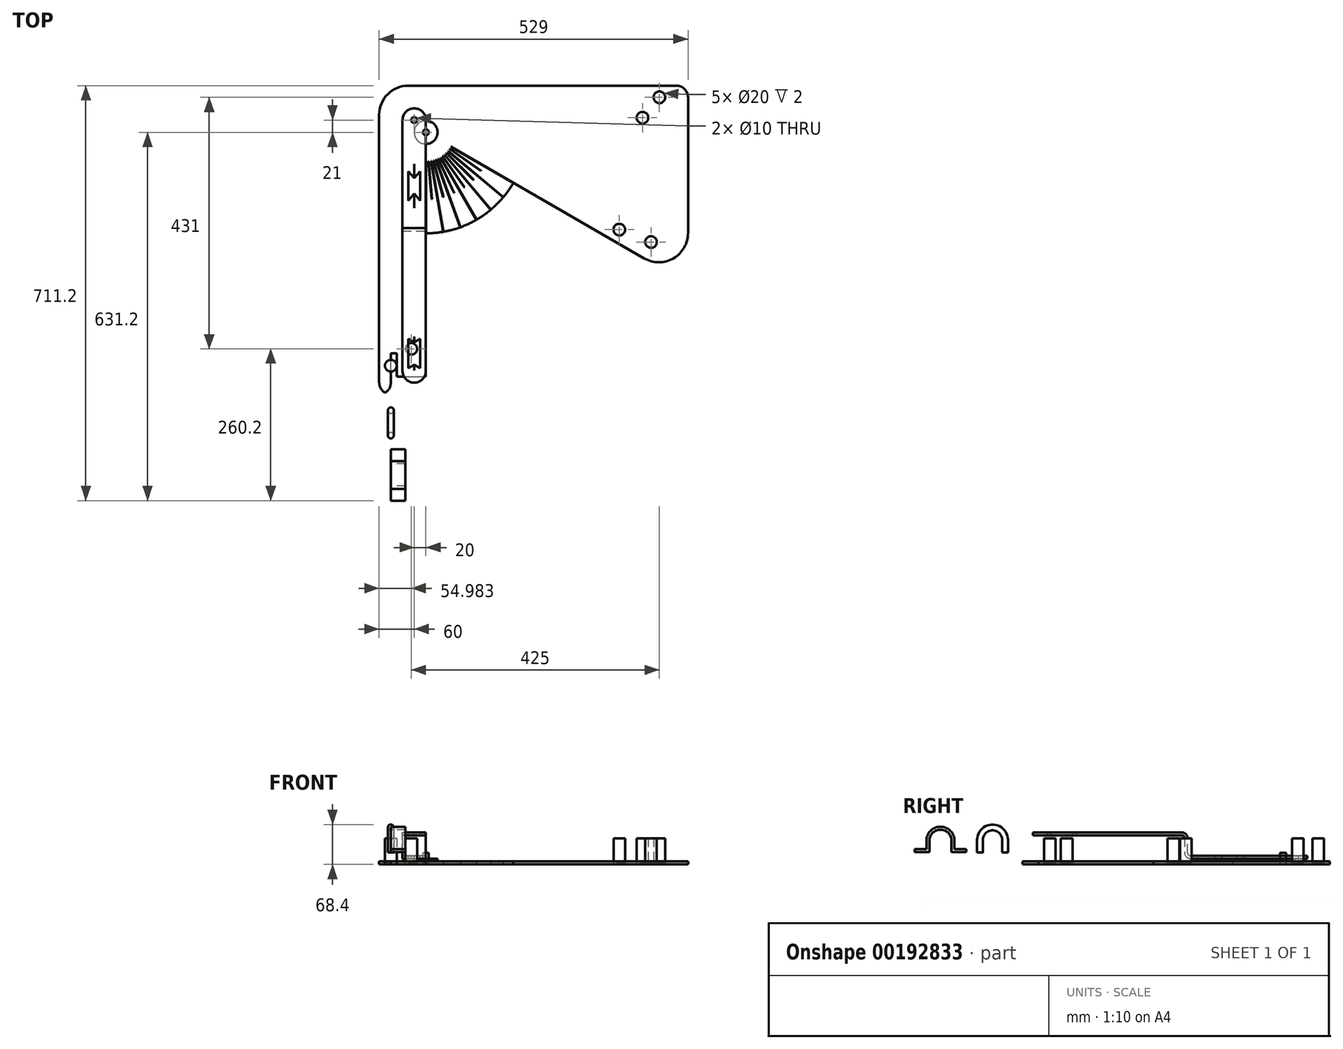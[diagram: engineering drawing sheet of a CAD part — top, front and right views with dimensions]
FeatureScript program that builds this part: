
annotation { "Feature Type Name" : "Feature", "Feature Type Description" : "" }
export const myFeature = defineFeature(function(context is Context, id is Id, definition is map)
    precondition{}
    {
        {
            var Q0;
            Q0=qCreatedBy(makeId("Top.planeOp"),FACE);
            var sketch = newSketch(context, id + "F0", { "sketchPlane" : qUnion([Q0])});
            skLineSegment(sketch, "E0.bottom", {"start": v(0, 0) * mm, "end": v(489, 0) * mm});
            skLineSegment(sketch, "E0.left", {"start": v(0, 0) * mm, "end": v(0, 500) * mm});
            skLineSegment(sketch, "E0.right", {"start": v(489, 0) * mm, "end": v(489, 479) * mm});
            skLineSegment(sketch, "E1.top", {"start": v(0, 0) * mm, "end": v(10, 0) * mm});
            skLineSegment(sketch, "E1.left", {"start": v(0, 489) * mm, "end": v(0, 0) * mm});
            skLineSegment(sketch, "E1.right", {"start": v(10, 50) * mm, "end": v(10, 10) * mm});
            skPoint(sketch, "E2", {"position": v(60, 429) * mm});
            skLineSegment(sketch, "E3", {"start": v(60, 255.9) * mm, "end": v(60, 0) * mm});
            skLineSegment(sketch, "E4", {"start": v(209.9, 342.45) * mm, "end": v(489, 181.32) * mm});
            skLineSegment(sketch, "E5.bottom", {"start": v(10, 48) * mm, "end": v(60, 48) * mm, "construction": true});
            skLineSegment(sketch, "E5.right", {"start": v(60, 48) * mm, "end": v(60, 10) * mm, "construction": true});
            skLineSegment(sketch, "E6.top", {"start": v(441, 429) * mm, "end": v(479, 429) * mm, "construction": true});
            skLineSegment(sketch, "E6.left", {"start": v(441, 479) * mm, "end": v(441, 429) * mm, "construction": true});
            skArc(sketch, "E7", {"start": v(60, 29) * mm, "mid": v(342.84, 146.16) * mm, "end": v(460, 429) * mm, "construction": true});
            skPoint(sketch, "E8", {"position": v(10, 29) * mm});
            skPoint(sketch, "E9", {"position": v(460, 479) * mm});
            skArc(sketch, "E10.0", {"start": v(60, 10) * mm, "mid": v(356.28, 132.72) * mm, "end": v(479, 429) * mm, "construction": true});
            skArc(sketch, "E11.0", {"start": v(60, 48) * mm, "mid": v(329.4, 159.6) * mm, "end": v(441, 429) * mm, "construction": true});
            skLineSegment(sketch, "E12", {"start": v(60, 255.9) * mm, "end": v(209.9, 342.45) * mm, "construction": true});
            skPoint(sketch, "E13.end.orphan", {"position": v(189.9, 354) * mm});
            skPoint(sketch, "E13.start.orphan", {"position": v(60, 279) * mm});
            skCircle(sketch, "E14", {"center": v(60, 429) * mm, "radius": 5 * mm});
            skLineSegment(sketch, "E15.top", {"start": v(489, 489) * mm, "end": v(0, 489) * mm});
            skLineSegment(sketch, "E15.left", {"start": v(489, 479) * mm, "end": v(489, 489) * mm});
            skLineSegment(sketch, "E16", {"start": v(439, 489) * mm, "end": v(439, 479) * mm});
            skLineSegment(sketch, "E17", {"start": v(439, 479) * mm, "end": v(479, 479) * mm});
            skLineSegment(sketch, "E18", {"start": v(479, 479) * mm, "end": v(479, 429) * mm});
            skLineSegment(sketch, "E19", {"start": v(489, 429) * mm, "end": v(479, 429) * mm});
            skArc(sketch, "E20", {"start": v(60, 255.9) * mm, "mid": v(146.55, 279.1) * mm, "end": v(209.9, 342.45) * mm});
            skLineSegment(sketch, "E21", {"start": v(0, 50) * mm, "end": v(10, 50) * mm});
            skLineSegment(sketch, "E22", {"start": v(10, 10) * mm, "end": v(60, 10) * mm});
            skLineSegment(sketch, "E23", {"start": v(60, 0) * mm, "end": v(60, -20) * mm});
            skLineSegment(sketch, "E24", {"start": v(60, -20) * mm, "end": v(0, -20) * mm});
            skLineSegment(sketch, "E25", {"start": v(0, -20) * mm, "end": v(0, 0) * mm});
            skLineSegment(sketch, "E26", {"start": v(0, 489) * mm, "end": v(-20, 489) * mm});
            skLineSegment(sketch, "E27", {"start": v(-20, 489) * mm, "end": v(-20, -20) * mm});
            skLineSegment(sketch, "E28", {"start": v(-20, -20) * mm, "end": v(0, -20) * mm});
            skLineSegment(sketch, "E29", {"start": v(489, 181.32) * mm, "end": v(509, 169.77) * mm});
            skLineSegment(sketch, "E30", {"start": v(509, 169.77) * mm, "end": v(509, 489) * mm});
            skLineSegment(sketch, "E31", {"start": v(509, 489) * mm, "end": v(489, 489) * mm});
            skLineSegment(sketch, "E32", {"start": v(509, 489) * mm, "end": v(509, 509) * mm});
            skLineSegment(sketch, "E33", {"start": v(509, 509) * mm, "end": v(-20, 509) * mm});
            skLineSegment(sketch, "E34", {"start": v(-20, 509) * mm, "end": v(-20, 489) * mm});
            skSolve(sketch);
        }
        {
            var Q0;
            {var subQ3=sQuery(id+"F0.wireOp",EDGE,"E1.right");Q0=makeQuery(id+"F0.imprint","IMPRINT",FACE,{"disambiguationData":[TD([[makeQuery(id+"F0.imprint","IMPRINT",EDGE,{"derivedFrom":subQ3}),1.0]])]});}
            var Q1;
            {var subQ2=sQuery(id+"F0.wireOp",EDGE,"E1.top");Q1=makeQuery(id+"F0.imprint","IMPRINT",FACE,{"disambiguationData":[TD([[makeQuery(id+"F0.imprint","IMPRINT",EDGE,{"derivedFrom":subQ2}),1.0]])]});}
            var Q2;
            {var subQ1=sQuery(id+"F0.wireOp",EDGE,"E15.left");Q2=makeQuery(id+"F0.imprint","IMPRINT",FACE,{"disambiguationData":[TD([[makeQuery(id+"F0.imprint","IMPRINT",EDGE,{"derivedFrom":subQ1}),1.0]])]});}
            var Q3;
            {var subQ1=sQuery(id+"F0.wireOp",EDGE,"E25");Q3=makeQuery(id+"F0.imprint","IMPRINT",FACE,{"disambiguationData":[TD([[makeQuery(id+"F0.imprint","IMPRINT",EDGE,{"derivedFrom":subQ1}),1.0]])]});}
            var Q4;
            {var subQ0=sQuery(id+"F0.wireOp",EDGE,"E1.top");Q4=makeQuery(id+"F0.imprint","IMPRINT",FACE,{"disambiguationData":[TD([[makeQuery(id+"F0.imprint","IMPRINT",EDGE,{"derivedFrom":subQ0}),-1.0]])]});}
            var Q5;
            {var subQ3=sQuery(id+"F0.wireOp",EDGE,"E26");Q5=makeQuery(id+"F0.imprint","IMPRINT",FACE,{"disambiguationData":[TD([[makeQuery(id+"F0.imprint","IMPRINT",EDGE,{"derivedFrom":subQ3}),-1.0]])]});}
            var Q6;
            {var subQ1=sQuery(id+"F0.wireOp",EDGE,"E15.left");Q6=makeQuery(id+"F0.imprint","IMPRINT",FACE,{"disambiguationData":[TD([[makeQuery(id+"F0.imprint","IMPRINT",EDGE,{"derivedFrom":subQ1}),-1.0]])]});}
            extrude(context, id + "F1", {"entities" : qUnion([Q0, Q1, Q2, Q3, Q4, Q5, Q6]), "depth" : 5 * mm});
        }
        {
            var Q0;
            Q0=makeQuery(id+"F1.opExtrude","SWEPT_FACE",FACE,{"disambiguationData":[OSD([sQuery(id+"F0.wireOp",EDGE,"E33")])]});
            cPlane(context, id + "F2", {"entities" : qUnion([Q0]), "cplaneType" : CPlaneType.OFFSET, "offset" : 80 * mm, "oppositeDirection" : true, "width" : 150 * mm, "height" : 150 * mm});
        }
        {
            var Q0;
            Q0=qCreatedBy(id+"F2.planeOp",FACE);
            var sketch = newSketch(context, id + "F3", { "sketchPlane" : qUnion([Q0])});
            skLineSegment(sketch, "E35", {"start": v(-60, 20) * mm, "end": v(-60, 0) * mm});
            skLineSegment(sketch, "E36", {"start": v(-60, 20) * mm, "end": v(-65, 20) * mm});
            skLineSegment(sketch, "E37", {"start": v(-65, 20) * mm, "end": v(-65, 10) * mm});
            skLineSegment(sketch, "E38", {"start": v(-65, 10) * mm, "end": v(-80, 10) * mm});
            skLineSegment(sketch, "E39", {"start": v(-80, 10) * mm, "end": v(-80, 5) * mm});
            skLineSegment(sketch, "E40", {"start": v(-80, 5) * mm, "end": v(-65, 5) * mm});
            skLineSegment(sketch, "E41", {"start": v(-65, 5) * mm, "end": v(-65, 0) * mm});
            skLineSegment(sketch, "E42", {"start": v(-65, 0) * mm, "end": v(-60, 0) * mm});
            skSolve(sketch);
        }
        {
            var Q0;
            Q0=qSketchRegion(id+"F3",true);
            var Q1;
            Q1=sQuery(id+"F3.wireOp",EDGE,"E35");
            revolve(context, id + "F4", {"entities" : qUnion([Q0]), "axis" : qUnion([Q1]), "revolveType" : RevolveType.FULL});
        }
        {
            var Q0;
            Q0=makeQuery(id+"F1.opExtrude","CAP_FACE",FACE,{"disambiguationData":[OSD([sQuery(id+"F0.wireOp",EDGE,"E0.bottom"),sQuery(id+"F0.wireOp",EDGE,"E0.top"),sQuery(id+"F0.wireOp",EDGE,"E0.right"),sQuery(id+"F0.wireOp",EDGE,"E1.right"),sQuery(id+"F0.wireOp",EDGE,"E3"),sQuery(id+"F0.wireOp",EDGE,"E4"),sQuery(id+"F0.wireOp",EDGE,"E12"),sQuery(id+"F0.wireOp",EDGE,"E14")])],"isStart":false});
            cPlane(context, id + "F5", {"entities" : qUnion([Q0]), "cplaneType" : CPlaneType.OFFSET, "offset" : 0 * mm, "width" : 150 * mm, "height" : 150 * mm});
        }
        {
            var Q0;
            Q0=qCreatedBy(id+"F5.planeOp",FACE);
            var sketch = newSketch(context, id + "F6", { "sketchPlane" : qUnion([Q0])});
            skCircle(sketch, "E43", {"center": v(34.98, 58) * mm, "radius": 10 * mm});
            skLineSegment(sketch, "E44.bottom", {"start": v(9.98, 10) * mm, "end": v(59.98, 10) * mm, "construction": true});
            skLineSegment(sketch, "E44.top", {"start": v(9.98, 48) * mm, "end": v(59.98, 48) * mm, "construction": true});
            skLineSegment(sketch, "E44.left", {"start": v(9.98, 10) * mm, "end": v(9.98, 48) * mm, "construction": true});
            skLineSegment(sketch, "E44.right", {"start": v(59.98, 10) * mm, "end": v(59.98, 48) * mm, "construction": true});
            skLineSegment(sketch, "E45.bottom", {"start": v(478.98, 479) * mm, "end": v(440.98, 479) * mm, "construction": true});
            skLineSegment(sketch, "E45.top", {"start": v(478.98, 429) * mm, "end": v(440.98, 429) * mm, "construction": true});
            skLineSegment(sketch, "E45.left", {"start": v(478.98, 479) * mm, "end": v(478.98, 429) * mm, "construction": true});
            skLineSegment(sketch, "E45.right", {"start": v(440.98, 479) * mm, "end": v(440.98, 429) * mm, "construction": true});
            skArc(sketch, "E46", {"start": v(59.98, 29) * mm, "mid": v(342.83, 146.16) * mm, "end": v(459.98, 429) * mm, "construction": true});
            skArc(sketch, "E47.0", {"start": v(59.98, 10) * mm, "mid": v(356.26, 132.72) * mm, "end": v(478.98, 429) * mm, "construction": true});
            skArc(sketch, "E48.0", {"start": v(59.98, 48) * mm, "mid": v(329.4, 159.6) * mm, "end": v(440.98, 429) * mm, "construction": true});
            skLineSegment(sketch, "E49", {"start": v(459.98, 429) * mm, "end": v(459.98, 479) * mm, "construction": true});
            skLineSegment(sketch, "E50", {"start": v(59.98, 29) * mm, "end": v(9.98, 29) * mm, "construction": true});
            skCircle(sketch, "E51", {"center": v(430.98, 454) * mm, "radius": 10 * mm});
            skCircle(sketch, "E52", {"center": v(445.6, 241.01) * mm, "radius": 10 * mm});
            skLineSegment(sketch, "E53", {"start": v(445.6, 241.01) * mm, "end": v(391.37, 262.2) * mm, "construction": true});
            skCircle(sketch, "E54", {"center": v(391.37, 262.2) * mm, "radius": 10 * mm});
            skCircle(sketch, "E55.MirrorC", {"center": v(34.98, 0) * mm, "radius": 10 * mm});
            skCircle(sketch, "E56", {"center": v(-0.02, 29) * mm, "radius": 10 * mm});
            skLineSegment(sketch, "E57", {"start": v(34.98, 0) * mm, "end": v(34.98, 48) * mm, "construction": true});
            skCircle(sketch, "E58.MirrorC", {"center": v(488.98, 454) * mm, "radius": 10 * mm});
            skLineSegment(sketch, "E59", {"start": v(430.98, 454) * mm, "end": v(488.98, 454) * mm, "construction": true});
            skCircle(sketch, "E60", {"center": v(459.98, 489) * mm, "radius": 10 * mm});
            skSolve(sketch);
        }
        {
            var Q0;
            Q0=makeQuery(id+"F6.imprint","IMPRINT",FACE,{"disambiguationData":[TD([[makeQuery(id+"F6.imprint","IMPRINT",EDGE,{"derivedFrom":sQuery(id+"F6.wireOp",EDGE,"E58.MirrorC")}),-1.0]])]});
            var Q1;
            Q1=makeQuery(id+"F6.imprint","IMPRINT",FACE,{"disambiguationData":[TD([[makeQuery(id+"F6.imprint","IMPRINT",EDGE,{"derivedFrom":sQuery(id+"F6.wireOp",EDGE,"E60")}),1.0]])]});
            var Q2;
            Q2=makeQuery(id+"F6.imprint","IMPRINT",FACE,{"disambiguationData":[TD([[makeQuery(id+"F6.imprint","IMPRINT",EDGE,{"derivedFrom":sQuery(id+"F6.wireOp",EDGE,"E51")}),1.0]])]});
            var Q3;
            Q3=makeQuery(id+"F6.imprint","IMPRINT",FACE,{"disambiguationData":[TD([[makeQuery(id+"F6.imprint","IMPRINT",EDGE,{"derivedFrom":sQuery(id+"F6.wireOp",EDGE,"E52")}),1.0]])]});
            var Q4;
            Q4=makeQuery(id+"F6.imprint","IMPRINT",FACE,{"disambiguationData":[TD([[makeQuery(id+"F6.imprint","IMPRINT",EDGE,{"derivedFrom":sQuery(id+"F6.wireOp",EDGE,"E54")}),1.0]])]});
            var Q5;
            Q5=makeQuery(id+"F6.imprint","IMPRINT",FACE,{"disambiguationData":[TD([[makeQuery(id+"F6.imprint","IMPRINT",EDGE,{"derivedFrom":sQuery(id+"F6.wireOp",EDGE,"E55.MirrorC")}),-1.0]])]});
            var Q6;
            Q6=makeQuery(id+"F6.imprint","IMPRINT",FACE,{"disambiguationData":[TD([[makeQuery(id+"F6.imprint","IMPRINT",EDGE,{"derivedFrom":sQuery(id+"F6.wireOp",EDGE,"E43")}),1.0]])]});
            var Q7;
            Q7=makeQuery(id+"F6.imprint","IMPRINT",FACE,{"disambiguationData":[TD([[makeQuery(id+"F6.imprint","IMPRINT",EDGE,{"derivedFrom":sQuery(id+"F6.wireOp",EDGE,"E56")}),1.0]])]});
            extrude(context, id + "F7", {"entities" : qUnion([Q0, Q1, Q2, Q3, Q4, Q5, Q6, Q7]), "operationType" : NewBodyOperationType.REMOVE, "oppositeDirection" : true, "depth" : 2 * mm});
        }
        {
            var Q0;
            Q0=makeQuery(id+"F6.imprint","IMPRINT",FACE,{"disambiguationData":[TD([[makeQuery(id+"F6.imprint","IMPRINT",EDGE,{"derivedFrom":sQuery(id+"F6.wireOp",EDGE,"E58.MirrorC")}),-1.0]])]});
            var Q1;
            Q1=makeQuery(id+"F6.imprint","IMPRINT",FACE,{"disambiguationData":[TD([[makeQuery(id+"F6.imprint","IMPRINT",EDGE,{"derivedFrom":sQuery(id+"F6.wireOp",EDGE,"E60")}),1.0]])]});
            var Q2;
            Q2=makeQuery(id+"F6.imprint","IMPRINT",FACE,{"disambiguationData":[TD([[makeQuery(id+"F6.imprint","IMPRINT",EDGE,{"derivedFrom":sQuery(id+"F6.wireOp",EDGE,"E51")}),1.0]])]});
            var Q3;
            Q3=makeQuery(id+"F6.imprint","IMPRINT",FACE,{"disambiguationData":[TD([[makeQuery(id+"F6.imprint","IMPRINT",EDGE,{"derivedFrom":sQuery(id+"F6.wireOp",EDGE,"E52")}),1.0]])]});
            var Q4;
            Q4=makeQuery(id+"F6.imprint","IMPRINT",FACE,{"disambiguationData":[TD([[makeQuery(id+"F6.imprint","IMPRINT",EDGE,{"derivedFrom":sQuery(id+"F6.wireOp",EDGE,"E54")}),1.0]])]});
            var Q5;
            Q5=makeQuery(id+"F6.imprint","IMPRINT",FACE,{"disambiguationData":[TD([[makeQuery(id+"F6.imprint","IMPRINT",EDGE,{"derivedFrom":sQuery(id+"F6.wireOp",EDGE,"E56")}),1.0]])]});
            var Q6;
            Q6=makeQuery(id+"F6.imprint","IMPRINT",FACE,{"disambiguationData":[TD([[makeQuery(id+"F6.imprint","IMPRINT",EDGE,{"derivedFrom":sQuery(id+"F6.wireOp",EDGE,"E55.MirrorC")}),-1.0]])]});
            var Q7;
            Q7=makeQuery(id+"F6.imprint","IMPRINT",FACE,{"disambiguationData":[TD([[makeQuery(id+"F6.imprint","IMPRINT",EDGE,{"derivedFrom":sQuery(id+"F6.wireOp",EDGE,"E43")}),1.0]])]});
            extrude(context, id + "F8", {"entities" : qUnion([Q0, Q1, Q2, Q3, Q4, Q5, Q6, Q7]), "depth" : 40 * mm});
        }
        {
            var Q0;
            Q0=makeQuery(id+"F1.opExtrude","CAP_FACE",FACE,{"disambiguationData":[OSD([sQuery(id+"F0.wireOp",EDGE,"E0.bottom"),sQuery(id+"F0.wireOp",EDGE,"E0.right"),sQuery(id+"F0.wireOp",EDGE,"E1.right"),sQuery(id+"F0.wireOp",EDGE,"E3"),sQuery(id+"F0.wireOp",EDGE,"E4"),sQuery(id+"F0.wireOp",EDGE,"E12"),sQuery(id+"F0.wireOp",EDGE,"E14"),sQuery(id+"F0.wireOp",EDGE,"E15.top"),sQuery(id+"F0.wireOp",EDGE,"E16"),sQuery(id+"F0.wireOp",EDGE,"E17"),sQuery(id+"F0.wireOp",EDGE,"E18"),sQuery(id+"F0.wireOp",EDGE,"E19")])],"isStart":false});
            var sketch = newSketch(context, id + "F9", { "sketchPlane" : qUnion([Q0])});
            skLineSegment(sketch, "E61", {"start": v(60, 379) * mm, "end": v(60, 255.9) * mm});
            skLineSegment(sketch, "E62", {"start": v(103.3, 404) * mm, "end": v(209.9, 342.45) * mm});
            skArc(sketch, "E63", {"start": v(60, 314) * mm, "mid": v(117.5, 329.4) * mm, "end": v(159.6, 371.5) * mm});
            skLineSegment(sketch, "E64.0", {"start": v(64.45, 426.72) * mm, "end": v(210.03, 342.67) * mm});
            skArc(sketch, "E65", {"start": v(60, 424) * mm, "mid": v(62.6, 424.73) * mm, "end": v(64.45, 426.72) * mm});
            skLineSegment(sketch, "E66.trimOffspring", {"start": v(64.2, 426.29) * mm, "end": v(64.83, 425.92) * mm});
            skLineSegment(sketch, "E67", {"start": v(210.03, 342.67) * mm, "end": v(209.9, 342.45) * mm});
            skLineSegment(sketch, "E68", {"start": v(100.96, 400.32) * mm, "end": v(154.2, 363.04) * mm});
            skLineSegment(sketch, "E69", {"start": v(98.3, 396.86) * mm, "end": v(192.6, 317.74) * mm});
            skLineSegment(sketch, "E70", {"start": v(95.36, 393.64) * mm, "end": v(141.32, 347.68) * mm});
            skLineSegment(sketch, "E71", {"start": v(92.14, 390.7) * mm, "end": v(171.26, 296.4) * mm});
            skLineSegment(sketch, "E72", {"start": v(88.68, 388.04) * mm, "end": v(125.96, 334.8) * mm});
            skLineSegment(sketch, "E73", {"start": v(85, 385.7) * mm, "end": v(146.55, 279.1) * mm});
            skLineSegment(sketch, "E74", {"start": v(81.13, 383.68) * mm, "end": v(108.6, 324.77) * mm});
            skLineSegment(sketch, "E75", {"start": v(77.1, 382.02) * mm, "end": v(119.2, 266.34) * mm});
            skLineSegment(sketch, "E76", {"start": v(72.94, 380.7) * mm, "end": v(89.76, 317.92) * mm});
            skLineSegment(sketch, "E77", {"start": v(68.68, 379.76) * mm, "end": v(90.06, 258.54) * mm});
            skLineSegment(sketch, "E78", {"start": v(64.36, 379.2) * mm, "end": v(70.02, 314.44) * mm});
            skArc(sketch, "E79", {"start": v(60, 255.9) * mm, "mid": v(146.55, 279.1) * mm, "end": v(209.9, 342.45) * mm, "construction": true});
            skPoint(sketch, "E80.orphan", {"position": v(117.5, 329.4) * mm});
            skLineSegment(sketch, "E81.0", {"start": v(64.24, 426.34) * mm, "end": v(64.83, 425.92) * mm});
            skLineSegment(sketch, "E82.0", {"start": v(63.95, 425.93) * mm, "end": v(64.55, 425.51) * mm});
            skLineSegment(sketch, "E83.0", {"start": v(63.67, 425.6) * mm, "end": v(64.23, 425.13) * mm});
            skLineSegment(sketch, "E84.0", {"start": v(64, 425.98) * mm, "end": v(64.55, 425.51) * mm});
            skLineSegment(sketch, "E85.0", {"start": v(63.36, 425.29) * mm, "end": v(63.87, 424.77) * mm});
            skLineSegment(sketch, "E86.0", {"start": v(63.71, 425.64) * mm, "end": v(64.23, 425.13) * mm});
            skLineSegment(sketch, "E87.0", {"start": v(63.02, 425) * mm, "end": v(63.49, 424.45) * mm});
            skLineSegment(sketch, "E88.0", {"start": v(63.4, 425.33) * mm, "end": v(63.87, 424.77) * mm});
            skLineSegment(sketch, "E89.0", {"start": v(63.07, 425.05) * mm, "end": v(63.49, 424.45) * mm});
            skLineSegment(sketch, "E90.0", {"start": v(62.66, 424.76) * mm, "end": v(63.08, 424.17) * mm});
            skLineSegment(sketch, "E91.0", {"start": v(55.7, 435.96) * mm, "end": v(62.65, 423.92) * mm});
            skLineSegment(sketch, "E92.0", {"start": v(56.12, 436.21) * mm, "end": v(63.08, 424.17) * mm});
            skLineSegment(sketch, "E93.0", {"start": v(61.89, 424.36) * mm, "end": v(62.2, 423.7) * mm});
            skLineSegment(sketch, "E94.0", {"start": v(62.34, 424.57) * mm, "end": v(62.65, 423.92) * mm});
            skLineSegment(sketch, "E95.0", {"start": v(61.48, 424.22) * mm, "end": v(61.72, 423.53) * mm});
            skLineSegment(sketch, "E96.0", {"start": v(61.95, 424.39) * mm, "end": v(62.2, 423.7) * mm});
            skLineSegment(sketch, "E97.0", {"start": v(61.05, 424.1) * mm, "end": v(61.24, 423.4) * mm});
            skLineSegment(sketch, "E98.0", {"start": v(61.54, 424.24) * mm, "end": v(61.72, 423.53) * mm});
            skLineSegment(sketch, "E99.0", {"start": v(60.62, 424.03) * mm, "end": v(60.75, 423.32) * mm});
            skLineSegment(sketch, "E100.0", {"start": v(61.11, 424.12) * mm, "end": v(61.24, 423.4) * mm});
            skLineSegment(sketch, "E101.0", {"start": v(60.19, 424) * mm, "end": v(60.25, 423.27) * mm});
            skLineSegment(sketch, "E102.0", {"start": v(60.68, 424.04) * mm, "end": v(60.75, 423.32) * mm});
            skLineSegment(sketch, "E103.0", {"start": v(59.75, 429) * mm, "end": v(59.75, 255.9) * mm});
            skLineSegment(sketch, "E104.0", {"start": v(60.25, 424) * mm, "end": v(60.25, 423.27) * mm});
            skArc(sketch, "E105", {"start": v(103.3, 404) * mm, "mid": v(85, 385.7) * mm, "end": v(60, 379) * mm});
            skLineSegment(sketch, "E106.trimOffspring", {"start": v(60.25, 379) * mm, "end": v(60.25, 255.9) * mm});
            skLineSegment(sketch, "E107.trimOffspring", {"start": v(64.1, 379.17) * mm, "end": v(69.77, 314.42) * mm});
            skLineSegment(sketch, "E108.trimOffspring", {"start": v(64.6, 379.21) * mm, "end": v(70.27, 314.46) * mm});
            skLineSegment(sketch, "E109.trimOffspring", {"start": v(68.44, 379.72) * mm, "end": v(89.81, 258.5) * mm});
            skLineSegment(sketch, "E110.trimOffspring", {"start": v(68.93, 379.8) * mm, "end": v(90.3, 258.58) * mm});
            skLineSegment(sketch, "E111.trimOffspring", {"start": v(72.7, 380.64) * mm, "end": v(89.52, 317.85) * mm});
            skLineSegment(sketch, "E112.trimOffspring", {"start": v(73.18, 380.77) * mm, "end": v(90, 317.98) * mm});
            skLineSegment(sketch, "E113.trimOffspring", {"start": v(76.87, 381.93) * mm, "end": v(118.97, 266.26) * mm});
            skLineSegment(sketch, "E114.trimOffspring", {"start": v(77.34, 382.1) * mm, "end": v(119.44, 266.43) * mm});
            skLineSegment(sketch, "E115.trimOffspring", {"start": v(80.9, 383.58) * mm, "end": v(108.37, 324.67) * mm});
            skLineSegment(sketch, "E116.trimOffspring", {"start": v(81.36, 383.8) * mm, "end": v(108.83, 324.88) * mm});
            skLineSegment(sketch, "E117.trimOffspring", {"start": v(88.47, 387.9) * mm, "end": v(125.76, 334.65) * mm});
            skLineSegment(sketch, "E118.trimOffspring", {"start": v(88.88, 388.19) * mm, "end": v(126.17, 334.94) * mm});
            skLineSegment(sketch, "E119.trimOffspring", {"start": v(84.78, 385.57) * mm, "end": v(146.33, 278.97) * mm});
            skLineSegment(sketch, "E120.trimOffspring", {"start": v(85.22, 385.82) * mm, "end": v(146.76, 279.22) * mm});
            skLineSegment(sketch, "E121.trimOffspring", {"start": v(91.95, 390.54) * mm, "end": v(171.07, 296.24) * mm});
            skLineSegment(sketch, "E122.trimOffspring", {"start": v(92.33, 390.86) * mm, "end": v(171.45, 296.56) * mm});
            skLineSegment(sketch, "E123.trimOffspring", {"start": v(95.18, 393.47) * mm, "end": v(141.14, 347.5) * mm});
            skLineSegment(sketch, "E124.trimOffspring", {"start": v(95.53, 393.82) * mm, "end": v(141.5, 347.86) * mm});
            skLineSegment(sketch, "E125.trimOffspring", {"start": v(98.14, 396.67) * mm, "end": v(192.44, 317.55) * mm});
            skLineSegment(sketch, "E126.trimOffspring", {"start": v(98.46, 397.05) * mm, "end": v(192.76, 317.93) * mm});
            skLineSegment(sketch, "E127.trimOffspring", {"start": v(100.81, 400.12) * mm, "end": v(154.06, 362.83) * mm});
            skLineSegment(sketch, "E128.trimOffspring", {"start": v(101.1, 400.53) * mm, "end": v(154.35, 363.24) * mm});
            skLineSegment(sketch, "E129.trimOffspring", {"start": v(103.18, 403.78) * mm, "end": v(209.78, 342.24) * mm});
            skArc(sketch, "E130", {"start": v(209.9, 342.45) * mm, "mid": v(146.55, 279.1) * mm, "end": v(60, 255.9) * mm});
            skSolve(sketch);
        }
        {
            var Q0;
            {var subQ0=sQuery(id+"F9.wireOp",EDGE,"E105");var subQ1=sQuery(id+"F9.wireOp",EDGE,"E62");var subQ2=makeQuery(id+"F9.imprint","INTERSECT",VERTEX,{"derivedFrom":[subQ1,subQ0]});Q0=makeQuery(id+"F9.imprint","IMPRINT",FACE,{"disambiguationData":[TD([[makeQuery(id+"F9.imprint","IMPRINT",EDGE,{"disambiguationData":[TD([[subQ2,-1.0]])],"derivedFrom":subQ1}),-1.0]])]});}
            var Q1;
            {var subQ0=sQuery(id+"F9.wireOp",EDGE,"E62");var subQ3=sQuery(id+"F9.wireOp",EDGE,"E63");var subQ4=makeQuery(id+"F9.imprint","INTERSECT",VERTEX,{"derivedFrom":[subQ0,subQ3]});Q1=makeQuery(id+"F9.imprint","IMPRINT",FACE,{"disambiguationData":[TD([[makeQuery(id+"F9.imprint","IMPRINT",EDGE,{"disambiguationData":[TD([[subQ4,1.0]])],"derivedFrom":subQ3}),-1.0]])]});}
            var Q2;
            {var subQ0=sQuery(id+"F9.wireOp",EDGE,"E68");Q2=makeQuery(id+"F9.imprint","IMPRINT",FACE,{"disambiguationData":[TD([[makeQuery(id+"F9.imprint","IMPRINT",EDGE,{"derivedFrom":subQ0}),1.0]])]});}
            var Q3;
            {var subQ0=sQuery(id+"F9.wireOp",EDGE,"E68");Q3=makeQuery(id+"F9.imprint","IMPRINT",FACE,{"disambiguationData":[TD([[makeQuery(id+"F9.imprint","IMPRINT",EDGE,{"derivedFrom":subQ0}),-1.0]])]});}
            var Q4;
            {var subQ0=sQuery(id+"F9.wireOp",EDGE,"E69");var subQ1=sQuery(id+"F9.wireOp",EDGE,"E63");var subQ2=makeQuery(id+"F9.imprint","INTERSECT",VERTEX,{"derivedFrom":[subQ1,subQ0]});Q4=makeQuery(id+"F9.imprint","IMPRINT",FACE,{"disambiguationData":[TD([[makeQuery(id+"F9.imprint","IMPRINT",EDGE,{"disambiguationData":[TD([[subQ2,-1.0]])],"derivedFrom":subQ1}),1.0]])]});}
            var Q5;
            {var subQ0=sQuery(id+"F9.wireOp",EDGE,"E125.trimOffspring");var subQ1=sQuery(id+"F9.wireOp",EDGE,"E63");var subQ2=makeQuery(id+"F9.imprint","INTERSECT",VERTEX,{"derivedFrom":[subQ1,subQ0]});Q5=makeQuery(id+"F9.imprint","IMPRINT",FACE,{"disambiguationData":[TD([[makeQuery(id+"F9.imprint","IMPRINT",EDGE,{"disambiguationData":[TD([[subQ2,-1.0]])],"derivedFrom":subQ1}),1.0]])]});}
            var Q6;
            {var subQ0=sQuery(id+"F9.wireOp",EDGE,"E125.trimOffspring");var subQ1=sQuery(id+"F9.wireOp",EDGE,"E63");var subQ2=makeQuery(id+"F9.imprint","INTERSECT",VERTEX,{"derivedFrom":[subQ1,subQ0]});Q6=makeQuery(id+"F9.imprint","IMPRINT",FACE,{"disambiguationData":[TD([[makeQuery(id+"F9.imprint","IMPRINT",EDGE,{"disambiguationData":[TD([[subQ2,-1.0]])],"derivedFrom":subQ1}),-1.0]])]});}
            var Q7;
            {var subQ0=sQuery(id+"F9.wireOp",EDGE,"E69");var subQ1=sQuery(id+"F9.wireOp",EDGE,"E63");var subQ2=makeQuery(id+"F9.imprint","INTERSECT",VERTEX,{"derivedFrom":[subQ1,subQ0]});Q7=makeQuery(id+"F9.imprint","IMPRINT",FACE,{"disambiguationData":[TD([[makeQuery(id+"F9.imprint","IMPRINT",EDGE,{"disambiguationData":[TD([[subQ2,-1.0]])],"derivedFrom":subQ1}),-1.0]])]});}
            var Q8;
            {var subQ0=sQuery(id+"F9.wireOp",EDGE,"E70");Q8=makeQuery(id+"F9.imprint","IMPRINT",FACE,{"disambiguationData":[TD([[makeQuery(id+"F9.imprint","IMPRINT",EDGE,{"derivedFrom":subQ0}),-1.0]])]});}
            var Q9;
            {var subQ0=sQuery(id+"F9.wireOp",EDGE,"E70");Q9=makeQuery(id+"F9.imprint","IMPRINT",FACE,{"disambiguationData":[TD([[makeQuery(id+"F9.imprint","IMPRINT",EDGE,{"derivedFrom":subQ0}),1.0]])]});}
            var Q10;
            {var subQ0=sQuery(id+"F9.wireOp",EDGE,"E71");var subQ1=sQuery(id+"F9.wireOp",EDGE,"E63");var subQ2=makeQuery(id+"F9.imprint","INTERSECT",VERTEX,{"derivedFrom":[subQ1,subQ0]});Q10=makeQuery(id+"F9.imprint","IMPRINT",FACE,{"disambiguationData":[TD([[makeQuery(id+"F9.imprint","IMPRINT",EDGE,{"disambiguationData":[TD([[subQ2,-1.0]])],"derivedFrom":subQ1}),1.0]])]});}
            var Q11;
            {var subQ0=sQuery(id+"F9.wireOp",EDGE,"E71");var subQ1=sQuery(id+"F9.wireOp",EDGE,"E63");var subQ2=makeQuery(id+"F9.imprint","INTERSECT",VERTEX,{"derivedFrom":[subQ1,subQ0]});Q11=makeQuery(id+"F9.imprint","IMPRINT",FACE,{"disambiguationData":[TD([[makeQuery(id+"F9.imprint","IMPRINT",EDGE,{"disambiguationData":[TD([[subQ2,-1.0]])],"derivedFrom":subQ1}),-1.0]])]});}
            var Q12;
            {var subQ0=sQuery(id+"F9.wireOp",EDGE,"E121.trimOffspring");var subQ1=sQuery(id+"F9.wireOp",EDGE,"E63");var subQ2=makeQuery(id+"F9.imprint","INTERSECT",VERTEX,{"derivedFrom":[subQ1,subQ0]});Q12=makeQuery(id+"F9.imprint","IMPRINT",FACE,{"disambiguationData":[TD([[makeQuery(id+"F9.imprint","IMPRINT",EDGE,{"disambiguationData":[TD([[subQ2,-1.0]])],"derivedFrom":subQ1}),-1.0]])]});}
            var Q13;
            {var subQ0=sQuery(id+"F9.wireOp",EDGE,"E121.trimOffspring");var subQ1=sQuery(id+"F9.wireOp",EDGE,"E63");var subQ2=makeQuery(id+"F9.imprint","INTERSECT",VERTEX,{"derivedFrom":[subQ1,subQ0]});Q13=makeQuery(id+"F9.imprint","IMPRINT",FACE,{"disambiguationData":[TD([[makeQuery(id+"F9.imprint","IMPRINT",EDGE,{"disambiguationData":[TD([[subQ2,-1.0]])],"derivedFrom":subQ1}),1.0]])]});}
            var Q14;
            {var subQ0=sQuery(id+"F9.wireOp",EDGE,"E72");Q14=makeQuery(id+"F9.imprint","IMPRINT",FACE,{"disambiguationData":[TD([[makeQuery(id+"F9.imprint","IMPRINT",EDGE,{"derivedFrom":subQ0}),1.0]])]});}
            var Q15;
            {var subQ0=sQuery(id+"F9.wireOp",EDGE,"E72");Q15=makeQuery(id+"F9.imprint","IMPRINT",FACE,{"disambiguationData":[TD([[makeQuery(id+"F9.imprint","IMPRINT",EDGE,{"derivedFrom":subQ0}),-1.0]])]});}
            var Q16;
            {var subQ0=sQuery(id+"F9.wireOp",EDGE,"E120.trimOffspring");var subQ1=sQuery(id+"F9.wireOp",EDGE,"E63");var subQ2=makeQuery(id+"F9.imprint","INTERSECT",VERTEX,{"derivedFrom":[subQ1,subQ0]});Q16=makeQuery(id+"F9.imprint","IMPRINT",FACE,{"disambiguationData":[TD([[makeQuery(id+"F9.imprint","IMPRINT",EDGE,{"disambiguationData":[TD([[subQ2,1.0]])],"derivedFrom":subQ1}),1.0]])]});}
            var Q17;
            {var subQ0=sQuery(id+"F9.wireOp",EDGE,"E119.trimOffspring");var subQ1=sQuery(id+"F9.wireOp",EDGE,"E63");var subQ2=makeQuery(id+"F9.imprint","INTERSECT",VERTEX,{"derivedFrom":[subQ1,subQ0]});Q17=makeQuery(id+"F9.imprint","IMPRINT",FACE,{"disambiguationData":[TD([[makeQuery(id+"F9.imprint","IMPRINT",EDGE,{"disambiguationData":[TD([[subQ2,-1.0]])],"derivedFrom":subQ1}),1.0]])]});}
            var Q18;
            {var subQ0=sQuery(id+"F9.wireOp",EDGE,"E74");Q18=makeQuery(id+"F9.imprint","IMPRINT",FACE,{"disambiguationData":[TD([[makeQuery(id+"F9.imprint","IMPRINT",EDGE,{"derivedFrom":subQ0}),-1.0]])]});}
            var Q19;
            {var subQ0=sQuery(id+"F9.wireOp",EDGE,"E74");Q19=makeQuery(id+"F9.imprint","IMPRINT",FACE,{"disambiguationData":[TD([[makeQuery(id+"F9.imprint","IMPRINT",EDGE,{"derivedFrom":subQ0}),1.0]])]});}
            var Q20;
            {var subQ0=sQuery(id+"F9.wireOp",EDGE,"E75");var subQ1=sQuery(id+"F9.wireOp",EDGE,"E63");var subQ2=makeQuery(id+"F9.imprint","INTERSECT",VERTEX,{"derivedFrom":[subQ1,subQ0]});Q20=makeQuery(id+"F9.imprint","IMPRINT",FACE,{"disambiguationData":[TD([[makeQuery(id+"F9.imprint","IMPRINT",EDGE,{"disambiguationData":[TD([[subQ2,-1.0]])],"derivedFrom":subQ1}),1.0]])]});}
            var Q21;
            {var subQ0=sQuery(id+"F9.wireOp",EDGE,"E113.trimOffspring");var subQ1=sQuery(id+"F9.wireOp",EDGE,"E63");var subQ2=makeQuery(id+"F9.imprint","INTERSECT",VERTEX,{"derivedFrom":[subQ1,subQ0]});Q21=makeQuery(id+"F9.imprint","IMPRINT",FACE,{"disambiguationData":[TD([[makeQuery(id+"F9.imprint","IMPRINT",EDGE,{"disambiguationData":[TD([[subQ2,-1.0]])],"derivedFrom":subQ1}),1.0]])]});}
            var Q22;
            {var subQ0=sQuery(id+"F9.wireOp",EDGE,"E113.trimOffspring");var subQ1=sQuery(id+"F9.wireOp",EDGE,"E63");var subQ2=makeQuery(id+"F9.imprint","INTERSECT",VERTEX,{"derivedFrom":[subQ1,subQ0]});Q22=makeQuery(id+"F9.imprint","IMPRINT",FACE,{"disambiguationData":[TD([[makeQuery(id+"F9.imprint","IMPRINT",EDGE,{"disambiguationData":[TD([[subQ2,-1.0]])],"derivedFrom":subQ1}),-1.0]])]});}
            var Q23;
            {var subQ0=sQuery(id+"F9.wireOp",EDGE,"E75");var subQ1=sQuery(id+"F9.wireOp",EDGE,"E63");var subQ2=makeQuery(id+"F9.imprint","INTERSECT",VERTEX,{"derivedFrom":[subQ1,subQ0]});Q23=makeQuery(id+"F9.imprint","IMPRINT",FACE,{"disambiguationData":[TD([[makeQuery(id+"F9.imprint","IMPRINT",EDGE,{"disambiguationData":[TD([[subQ2,-1.0]])],"derivedFrom":subQ1}),-1.0]])]});}
            var Q24;
            {var subQ0=sQuery(id+"F9.wireOp",EDGE,"E76");Q24=makeQuery(id+"F9.imprint","IMPRINT",FACE,{"disambiguationData":[TD([[makeQuery(id+"F9.imprint","IMPRINT",EDGE,{"derivedFrom":subQ0}),1.0]])]});}
            var Q25;
            {var subQ0=sQuery(id+"F9.wireOp",EDGE,"E76");Q25=makeQuery(id+"F9.imprint","IMPRINT",FACE,{"disambiguationData":[TD([[makeQuery(id+"F9.imprint","IMPRINT",EDGE,{"derivedFrom":subQ0}),-1.0]])]});}
            var Q26;
            {var subQ0=sQuery(id+"F9.wireOp",EDGE,"E77");var subQ1=sQuery(id+"F9.wireOp",EDGE,"E63");var subQ2=makeQuery(id+"F9.imprint","INTERSECT",VERTEX,{"derivedFrom":[subQ1,subQ0]});Q26=makeQuery(id+"F9.imprint","IMPRINT",FACE,{"disambiguationData":[TD([[makeQuery(id+"F9.imprint","IMPRINT",EDGE,{"disambiguationData":[TD([[subQ2,-1.0]])],"derivedFrom":subQ1}),1.0]])]});}
            var Q27;
            {var subQ0=sQuery(id+"F9.wireOp",EDGE,"E109.trimOffspring");var subQ1=sQuery(id+"F9.wireOp",EDGE,"E63");var subQ2=makeQuery(id+"F9.imprint","INTERSECT",VERTEX,{"derivedFrom":[subQ1,subQ0]});Q27=makeQuery(id+"F9.imprint","IMPRINT",FACE,{"disambiguationData":[TD([[makeQuery(id+"F9.imprint","IMPRINT",EDGE,{"disambiguationData":[TD([[subQ2,-1.0]])],"derivedFrom":subQ1}),1.0]])]});}
            var Q28;
            {var subQ0=sQuery(id+"F9.wireOp",EDGE,"E109.trimOffspring");var subQ1=sQuery(id+"F9.wireOp",EDGE,"E63");var subQ2=makeQuery(id+"F9.imprint","INTERSECT",VERTEX,{"derivedFrom":[subQ1,subQ0]});Q28=makeQuery(id+"F9.imprint","IMPRINT",FACE,{"disambiguationData":[TD([[makeQuery(id+"F9.imprint","IMPRINT",EDGE,{"disambiguationData":[TD([[subQ2,-1.0]])],"derivedFrom":subQ1}),-1.0]])]});}
            var Q29;
            {var subQ0=sQuery(id+"F9.wireOp",EDGE,"E77");var subQ1=sQuery(id+"F9.wireOp",EDGE,"E63");var subQ2=makeQuery(id+"F9.imprint","INTERSECT",VERTEX,{"derivedFrom":[subQ1,subQ0]});Q29=makeQuery(id+"F9.imprint","IMPRINT",FACE,{"disambiguationData":[TD([[makeQuery(id+"F9.imprint","IMPRINT",EDGE,{"disambiguationData":[TD([[subQ2,-1.0]])],"derivedFrom":subQ1}),-1.0]])]});}
            var Q30;
            {var subQ0=sQuery(id+"F9.wireOp",EDGE,"E78");Q30=makeQuery(id+"F9.imprint","IMPRINT",FACE,{"disambiguationData":[TD([[makeQuery(id+"F9.imprint","IMPRINT",EDGE,{"derivedFrom":subQ0}),1.0]])]});}
            var Q31;
            {var subQ0=sQuery(id+"F9.wireOp",EDGE,"E78");Q31=makeQuery(id+"F9.imprint","IMPRINT",FACE,{"disambiguationData":[TD([[makeQuery(id+"F9.imprint","IMPRINT",EDGE,{"derivedFrom":subQ0}),-1.0]])]});}
            var Q32;
            {var subQ6=sQuery(id+"F9.wireOp",EDGE,"E61");Q32=makeQuery(id+"F9.imprint","IMPRINT",FACE,{"disambiguationData":[TD([[makeQuery(id+"F9.imprint","IMPRINT",EDGE,{"derivedFrom":subQ6}),1.0]])]});}
            var Q33;
            {var subQ0=sQuery(id+"F9.wireOp",EDGE,"E119.trimOffspring");var subQ1=sQuery(id+"F9.wireOp",EDGE,"E63");var subQ2=makeQuery(id+"F9.imprint","INTERSECT",VERTEX,{"derivedFrom":[subQ1,subQ0]});Q33=makeQuery(id+"F9.imprint","IMPRINT",FACE,{"disambiguationData":[TD([[makeQuery(id+"F9.imprint","IMPRINT",EDGE,{"disambiguationData":[TD([[subQ2,-1.0]])],"derivedFrom":subQ1}),-1.0]])]});}
            var Q34;
            {var subQ0=sQuery(id+"F9.wireOp",EDGE,"E73");var subQ1=sQuery(id+"F9.wireOp",EDGE,"E63");var subQ2=makeQuery(id+"F9.imprint","INTERSECT",VERTEX,{"derivedFrom":[subQ1,subQ0]});Q34=makeQuery(id+"F9.imprint","IMPRINT",FACE,{"disambiguationData":[TD([[makeQuery(id+"F9.imprint","IMPRINT",EDGE,{"disambiguationData":[TD([[subQ2,-1.0]])],"derivedFrom":subQ1}),-1.0]])]});}
            extrude(context, id + "F10", {"entities" : qUnion([Q0, Q1, Q2, Q3, Q4, Q5, Q6, Q7, Q8, Q9, Q10, Q11, Q12, Q13, Q14, Q15, Q16, Q17, Q18, Q19, Q20, Q21, Q22, Q23, Q24, Q25, Q26, Q27, Q28, Q29, Q30, Q31, Q32, Q33, Q34]), "operationType" : NewBodyOperationType.REMOVE, "oppositeDirection" : true, "depth" : 0.5 * mm});
        }
        {
            var Q0;
            Q0=makeQuery(id+"F10.boolean.opBoolean","MERGE",FACE,{"derivedFrom":[makeQuery(id+"F1.opExtrude","SWEPT_FACE",FACE,{"disambiguationData":[OSD([sQuery(id+"F0.wireOp",EDGE,"E3")])]}),makeQuery(id+"F10.opExtrude","SWEPT_FACE",FACE,{"disambiguationData":[OSD([sQuery(id+"F9.wireOp",EDGE,"E61")])]})]});
            var sketch = newSketch(context, id + "F11", { "sketchPlane" : qUnion([Q0])});
            skLineSegment(sketch, "E131.bottom", {"start": v(470, 10) * mm, "end": v(260, 10) * mm});
            skLineSegment(sketch, "E131.top", {"start": v(470, 15) * mm, "end": v(265, 15) * mm});
            skLineSegment(sketch, "E131.left", {"start": v(470, 10) * mm, "end": v(470, 15) * mm});
            skLineSegment(sketch, "E132", {"start": v(265, 15) * mm, "end": v(265, 55) * mm});
            skLineSegment(sketch, "E133", {"start": v(265, 55) * mm, "end": v(0, 55) * mm});
            skLineSegment(sketch, "E134", {"start": v(0, 55) * mm, "end": v(0, 50) * mm});
            skLineSegment(sketch, "E135", {"start": v(0, 50) * mm, "end": v(260, 50) * mm});
            skLineSegment(sketch, "E136", {"start": v(260, 50) * mm, "end": v(260, 10) * mm});
            skPoint(sketch, "E137.trimOffspring.end.orphan", {"position": v(0, 35) * mm});
            skSolve(sketch);
        }
        {
            var Q0;
            Q0=qSketchRegion(id+"F11",true);
            extrude(context, id + "F12", {"entities" : qUnion([Q0]), "oppositeDirection" : true, "depth" : 40 * mm});
        }
        {
            var Q0;
            Q0=makeQuery(id+"F12.opExtrude","SWEPT_FACE",FACE,{"disambiguationData":[OSD([sQuery(id+"F11.wireOp",EDGE,"E131.top")])]});
            var sketch = newSketch(context, id + "F13", { "sketchPlane" : qUnion([Q0])});
            skCircle(sketch, "E138", {"center": v(40, 450) * mm, "radius": 5 * mm});
            skPoint(sketch, "E138.centerSnap0", {"position": v(40, 470) * mm});
            skSolve(sketch);
        }
        {
            var Q0;
            Q0=qSketchRegion(id+"F13",true);
            extrude(context, id + "F14", {"entities" : qUnion([Q0]), "operationType" : NewBodyOperationType.REMOVE, "oppositeDirection" : true, "depth" : 10 * mm});
        }
        {
            var Q0;
            Q0=makeQuery(id+"F12.opExtrude","SWEPT_FACE",FACE,{"disambiguationData":[OSD([sQuery(id+"F11.wireOp",EDGE,"E131.top")])]});
            var sketch = newSketch(context, id + "F15", { "sketchPlane" : qUnion([Q0])});
            skLineSegment(sketch, "E139.bottom", {"start": v(30, 362.1) * mm, "end": v(50, 362.1) * mm});
            skLineSegment(sketch, "E139.top", {"start": v(30, 312.1) * mm, "end": v(50, 312.1) * mm});
            skLineSegment(sketch, "E139.left", {"start": v(30, 362.1) * mm, "end": v(30, 312.1) * mm});
            skLineSegment(sketch, "E139.right", {"start": v(50, 362.1) * mm, "end": v(50, 312.1) * mm});
            skPoint(sketch, "E139.middle", {"position": v(40, 337.1) * mm});
            skPoint(sketch, "E139.middle.positionSnap0", {"position": v(40, 470) * mm});
            skPoint(sketch, "E139.centerSnap0", {"position": v(40, 470) * mm});
            skLineSegment(sketch, "E140", {"start": v(30, 362.1) * mm, "end": v(40, 350.1) * mm});
            skLineSegment(sketch, "E141", {"start": v(40, 350.1) * mm, "end": v(50, 362.1) * mm});
            skLineSegment(sketch, "E142", {"start": v(30, 312.1) * mm, "end": v(40, 324.1) * mm});
            skPoint(sketch, "E142.endSnap0", {"position": v(40, 312.1) * mm});
            skLineSegment(sketch, "E143", {"start": v(40, 324.1) * mm, "end": v(50, 312.1) * mm});
            skSolve(sketch);
        }
        {
            var Q0;
            Q0=makeQuery(id+"F15.imprint","IMPRINT",FACE,{"disambiguationData":[TD([[makeQuery(id+"F15.imprint","IMPRINT",EDGE,{"derivedFrom":sQuery(id+"F15.wireOp",EDGE,"E139.left")}),1.0]])]});
            extrude(context, id + "F16", {"entities" : qUnion([Q0]), "operationType" : NewBodyOperationType.REMOVE, "oppositeDirection" : true, "depth" : 10 * mm});
        }
        {
            var Q0;
            Q0=makeQuery(id+"F12.opExtrude","SWEPT_FACE",FACE,{"disambiguationData":[OSD([sQuery(id+"F11.wireOp",EDGE,"E133")])]});
            var sketch = newSketch(context, id + "F17", { "sketchPlane" : qUnion([Q0])});
            skLineSegment(sketch, "E144.bottom", {"start": v(30, 75) * mm, "end": v(50, 75) * mm});
            skLineSegment(sketch, "E144.top", {"start": v(30, 25) * mm, "end": v(50, 25) * mm});
            skLineSegment(sketch, "E144.left", {"start": v(30, 75) * mm, "end": v(30, 25) * mm});
            skLineSegment(sketch, "E144.right", {"start": v(50, 75) * mm, "end": v(50, 25) * mm});
            skPoint(sketch, "E144.middle", {"position": v(40, 50) * mm});
            skPoint(sketch, "E144.middle.positionSnap0", {"position": v(40, 0) * mm});
            skPoint(sketch, "E144.centerSnap0", {"position": v(40, 0) * mm});
            skLineSegment(sketch, "E145", {"start": v(30, 75) * mm, "end": v(40, 69) * mm});
            skPoint(sketch, "E145.endSnap0", {"position": v(40, 25) * mm});
            skLineSegment(sketch, "E146", {"start": v(40, 69) * mm, "end": v(50, 75) * mm});
            skLineSegment(sketch, "E147", {"start": v(30, 25) * mm, "end": v(40, 31) * mm});
            skLineSegment(sketch, "E148", {"start": v(40, 31) * mm, "end": v(50, 25) * mm});
            skSolve(sketch);
        }
        {
            var Q0;
            Q0=makeQuery(id+"F17.imprint","IMPRINT",FACE,{"disambiguationData":[TD([[makeQuery(id+"F17.imprint","IMPRINT",EDGE,{"derivedFrom":sQuery(id+"F17.wireOp",EDGE,"E144.left")}),1.0]])]});
            extrude(context, id + "F18", {"entities" : qUnion([Q0]), "operationType" : NewBodyOperationType.REMOVE, "oppositeDirection" : true, "depth" : 10 * mm});
        }
        {
            var Q0;
            Q0=makeQuery(id+"F12.opExtrude","SWEPT_FACE",FACE,{"disambiguationData":[OSD([sQuery(id+"F11.wireOp",EDGE,"E131.top")])]});
            var sketch = newSketch(context, id + "F19", { "sketchPlane" : qUnion([Q0])});
            skLineSegment(sketch, "E149", {"start": v(40, 350.1) * mm, "end": v(40, 375.1) * mm});
            skLineSegment(sketch, "E150", {"start": v(40, 375.1) * mm, "end": v(40.25, 375.1) * mm});
            skLineSegment(sketch, "E151", {"start": v(40.25, 375.1) * mm, "end": v(40.25, 350.4) * mm});
            skLineSegment(sketch, "E152", {"start": v(40, 375.1) * mm, "end": v(39.75, 375.1) * mm});
            skLineSegment(sketch, "E153", {"start": v(39.75, 375.1) * mm, "end": v(39.75, 350.4) * mm});
            skLineSegment(sketch, "E154", {"start": v(39.75, 350.4) * mm, "end": v(40, 350.1) * mm});
            skLineSegment(sketch, "E155", {"start": v(40.25, 350.4) * mm, "end": v(40, 350.1) * mm});
            skLineSegment(sketch, "E156", {"start": v(40, 324.1) * mm, "end": v(40, 299.1) * mm});
            skLineSegment(sketch, "E157", {"start": v(40, 299.1) * mm, "end": v(40.25, 299.1) * mm});
            skLineSegment(sketch, "E158", {"start": v(40.25, 299.1) * mm, "end": v(40.25, 323.8) * mm});
            skLineSegment(sketch, "E159", {"start": v(40.25, 323.8) * mm, "end": v(40, 324.1) * mm});
            skLineSegment(sketch, "E160", {"start": v(40, 299.1) * mm, "end": v(39.75, 299.1) * mm});
            skLineSegment(sketch, "E161", {"start": v(39.75, 299.1) * mm, "end": v(39.75, 323.8) * mm});
            skLineSegment(sketch, "E162", {"start": v(39.75, 323.8) * mm, "end": v(40, 324.1) * mm});
            skSolve(sketch);
        }
        {
            var Q0;
            Q0=qSketchRegion(id+"F19",true);
            extrude(context, id + "F20", {"entities" : qUnion([Q0]), "operationType" : NewBodyOperationType.REMOVE, "oppositeDirection" : true, "depth" : 0.5 * mm});
        }
        {
            var Q0;
            Q0=makeQuery(id+"F12.opExtrude","SWEPT_FACE",FACE,{"disambiguationData":[OSD([sQuery(id+"F11.wireOp",EDGE,"E133")])]});
            var sketch = newSketch(context, id + "F21", { "sketchPlane" : qUnion([Q0])});
            skLineSegment(sketch, "E163", {"start": v(40, 69) * mm, "end": v(40, 79) * mm});
            skLineSegment(sketch, "E164", {"start": v(40, 79) * mm, "end": v(40.25, 79) * mm});
            skLineSegment(sketch, "E165", {"start": v(40.25, 79) * mm, "end": v(40.25, 69.15) * mm});
            skLineSegment(sketch, "E166", {"start": v(40.25, 69.15) * mm, "end": v(40, 69) * mm});
            skLineSegment(sketch, "E167", {"start": v(40, 79) * mm, "end": v(39.75, 79) * mm});
            skLineSegment(sketch, "E168", {"start": v(39.75, 79) * mm, "end": v(39.75, 69.15) * mm});
            skLineSegment(sketch, "E169", {"start": v(39.75, 69.15) * mm, "end": v(40, 69) * mm});
            skLineSegment(sketch, "E170", {"start": v(40, 31) * mm, "end": v(40, 21) * mm});
            skLineSegment(sketch, "E171", {"start": v(40, 21) * mm, "end": v(40.25, 21) * mm});
            skLineSegment(sketch, "E172", {"start": v(40.25, 21) * mm, "end": v(40.25, 30.85) * mm});
            skLineSegment(sketch, "E173", {"start": v(40.25, 30.85) * mm, "end": v(40, 31) * mm});
            skLineSegment(sketch, "E174", {"start": v(40, 21) * mm, "end": v(39.75, 21) * mm});
            skLineSegment(sketch, "E175", {"start": v(39.75, 21) * mm, "end": v(39.75, 30.85) * mm});
            skLineSegment(sketch, "E176", {"start": v(39.75, 30.85) * mm, "end": v(40, 31) * mm});
            skSolve(sketch);
        }
        {
            var Q0;
            Q0=qSketchRegion(id+"F21",true);
            extrude(context, id + "F22", {"entities" : qUnion([Q0]), "operationType" : NewBodyOperationType.REMOVE, "oppositeDirection" : true, "depth" : 0.25 * mm});
        }
        {
            var Q0;
            Q0=makeQuery(id+"F1.opExtrude","SWEPT_EDGE",EDGE,{"disambiguationData":[OSD([sQuery(id+"F0.wireOp",EDGE,"E33"),sQuery(id+"F0.wireOp",EDGE,"E34")])]});
            var Q1;
            Q1=makeQuery(id+"F1.opExtrude","SWEPT_EDGE",EDGE,{"disambiguationData":[OSD([sQuery(id+"F0.wireOp",EDGE,"E29"),sQuery(id+"F0.wireOp",EDGE,"E30")])]});
            fillet(context, id + "F23", {"entities" : qUnion([Q0, Q1]), "radius" : 50 * mm, "tangentPropagation" : true, "allowEdgeOverflow" : false});
        }
        {
            var Q0;
            Q0=makeQuery(id+"F1.opExtrude","SWEPT_EDGE",EDGE,{"disambiguationData":[OSD([sQuery(id+"F0.wireOp",EDGE,"E27"),sQuery(id+"F0.wireOp",EDGE,"E28")])]});
            var Q1;
            Q1=makeQuery(id+"F1.opExtrude","SWEPT_EDGE",EDGE,{"disambiguationData":[OSD([sQuery(id+"F0.wireOp",EDGE,"E32"),sQuery(id+"F0.wireOp",EDGE,"E33")])]});
            var Q2;
            Q2=makeQuery(id+"F1.opExtrude","SWEPT_EDGE",EDGE,{"disambiguationData":[OSD([sQuery(id+"F0.wireOp",EDGE,"E23"),sQuery(id+"F0.wireOp",EDGE,"E24")])]});
            fillet(context, id + "F24", {"entities" : qUnion([Q0, Q1, Q2]), "radius" : 20 * mm, "tangentPropagation" : true, "allowEdgeOverflow" : false});
        }
        {
            var Q0;
            Q0=makeQuery(id+"F12.opExtrude","CAP_EDGE",EDGE,{"disambiguationData":[OSD([sQuery(id+"F11.wireOp",EDGE,"E134")])],"isStart":true});
            var Q1;
            Q1=makeQuery(id+"F12.opExtrude","CAP_EDGE",EDGE,{"disambiguationData":[OSD([sQuery(id+"F11.wireOp",EDGE,"E134")])],"isStart":false});
            var Q2;
            Q2=makeQuery(id+"F12.opExtrude","CAP_EDGE",EDGE,{"disambiguationData":[OSD([sQuery(id+"F11.wireOp",EDGE,"E131.left")])],"isStart":false});
            var Q3;
            Q3=makeQuery(id+"F12.opExtrude","CAP_EDGE",EDGE,{"disambiguationData":[OSD([sQuery(id+"F11.wireOp",EDGE,"E131.left")])],"isStart":true});
            fillet(context, id + "F25", {"entities" : qUnion([Q0, Q1, Q2, Q3]), "radius" : 20 * mm, "tangentPropagation" : true, "allowEdgeOverflow" : false});
        }
        {
            var Q0;
            Q0=makeQuery(id+"F12.opExtrude","SWEPT_EDGE",EDGE,{"disambiguationData":[OSD([sQuery(id+"F11.wireOp",EDGE,"E132"),sQuery(id+"F11.wireOp",EDGE,"E133")])]});
            var Q1;
            Q1=makeQuery(id+"F12.opExtrude","SWEPT_EDGE",EDGE,{"disambiguationData":[OSD([sQuery(id+"F11.wireOp",EDGE,"E131.bottom"),sQuery(id+"F11.wireOp",EDGE,"E136")])]});
            fillet(context, id + "F26", {"entities" : qUnion([Q0, Q1]), "radius" : 10 * mm, "tangentPropagation" : true, "allowEdgeOverflow" : false});
        }
        {
            var Q0;
            Q0=makeQuery(id+"F12.opExtrude","SWEPT_EDGE",EDGE,{"disambiguationData":[OSD([sQuery(id+"F11.wireOp",EDGE,"E131.top"),sQuery(id+"F11.wireOp",EDGE,"E132")])]});
            var Q1;
            Q1=makeQuery(id+"F12.opExtrude","SWEPT_EDGE",EDGE,{"disambiguationData":[OSD([sQuery(id+"F11.wireOp",EDGE,"E135"),sQuery(id+"F11.wireOp",EDGE,"E136")])]});
            fillet(context, id + "F27", {"entities" : qUnion([Q0, Q1]), "radius" : 5 * mm, "tangentPropagation" : true, "allowEdgeOverflow" : false});
        }
        {
            var Q0;
            Q0=qCreatedBy(makeId("Right.planeOp"),FACE);
            var sketch = newSketch(context, id + "F28", { "sketchPlane" : qUnion([Q0])});
            skArc(sketch, "E177", {"start": v(-47.48, 41.9) * mm, "mid": v(-68.98, 63.4) * mm, "end": v(-90.48, 41.9) * mm});
            skLineSegment(sketch, "E178", {"start": v(-47.48, 41.9) * mm, "end": v(-47.48, 20.4) * mm});
            skLineSegment(sketch, "E179", {"start": v(-90.48, 41.9) * mm, "end": v(-90.48, 20.4) * mm});
            skSolve(sketch);
        }
        {
            var Q0;
            Q0=sQuery(id+"F28.wireOp",VERTEX,"E179.end");
            var Q1;
            Q1=qCreatedBy(makeId("Top.planeOp"),FACE);
            cPlane(context, id + "F29", {"entities" : qUnion([Q0, Q1]), "cplaneType" : CPlaneType.PLANE_POINT, "offset" : 25 * mm, "width" : 150 * mm, "height" : 150 * mm});
        }
        {
            var Q0;
            Q0=qCreatedBy(id+"F29.planeOp",FACE);
            var sketch = newSketch(context, id + "F30", { "sketchPlane" : qUnion([Q0])});
            skCircle(sketch, "E180", {"center": v(0, -90.48) * mm, "radius": 5 * mm});
            skSolve(sketch);
        }
        {
            var Q0;
            Q0=makeQuery(id+"F30.imprint","IMPRINT",FACE,{"disambiguationData":[TD([[makeQuery(id+"F30.imprint","IMPRINT",EDGE,{"derivedFrom":sQuery(id+"F30.wireOp",EDGE,"E180")}),1.0]])]});
            var Q1;
            Q1=sQuery(id+"F28.wireOp",EDGE,"E179");
            var Q2;
            Q2=sQuery(id+"F28.wireOp",EDGE,"E177");
            var Q3;
            Q3=sQuery(id+"F28.wireOp",EDGE,"E178");
            sweep(context, id + "F31", {"profiles" : qUnion([Q0]), "path" : qUnion([Q1, Q2, Q3])});
        }
        {
            var Q0;
            Q0=qCreatedBy(makeId("Right.planeOp"),FACE);
            var sketch = newSketch(context, id + "F32", { "sketchPlane" : qUnion([Q0])});
            skLineSegment(sketch, "E181", {"start": v(-114.2, 20.99) * mm, "end": v(-139.2, 20.99) * mm});
            skArc(sketch, "E182", {"start": v(-139.2, 40.56) * mm, "mid": v(-158.2, 59.56) * mm, "end": v(-177.2, 40.56) * mm});
            skArc(sketch, "E183.0", {"start": v(-134.2, 40.56) * mm, "mid": v(-158.2, 64.56) * mm, "end": v(-182.2, 40.56) * mm});
            skLineSegment(sketch, "E184.left", {"start": v(-139.2, 40.56) * mm, "end": v(-139.2, 20.99) * mm});
            skLineSegment(sketch, "E184.right", {"start": v(-134.2, 40.56) * mm, "end": v(-134.2, 26.56) * mm});
            skLineSegment(sketch, "E185.left", {"start": v(-177.2, 40.56) * mm, "end": v(-177.2, 20.99) * mm});
            skLineSegment(sketch, "E185.right", {"start": v(-182.2, 40.56) * mm, "end": v(-182.2, 26.56) * mm});
            skLineSegment(sketch, "E186", {"start": v(-134.2, 26.56) * mm, "end": v(-114.2, 26.56) * mm});
            skLineSegment(sketch, "E187", {"start": v(-114.2, 26.56) * mm, "end": v(-114.2, 20.99) * mm});
            skLineSegment(sketch, "E188", {"start": v(-182.2, 26.56) * mm, "end": v(-202.2, 26.56) * mm});
            skLineSegment(sketch, "E189", {"start": v(-202.2, 26.56) * mm, "end": v(-202.2, 20.99) * mm});
            skPoint(sketch, "E190.orphan", {"position": v(-139.2, 16.56) * mm});
            skLineSegment(sketch, "E191.trimOffspring", {"start": v(-177.2, 20.99) * mm, "end": v(-220.09, 20.99) * mm});
            skPoint(sketch, "E192.trimOffspring.end.orphan", {"position": v(-182.2, 16.56) * mm});
            skSolve(sketch);
        }
        {
            var Q0;
            Q0 = qSketchRegion(id + "F32", true);
            extrude(context, id + "F33", {"entities" : qUnion([Q0]), "depth" : 25 * mm});
        }
    });
